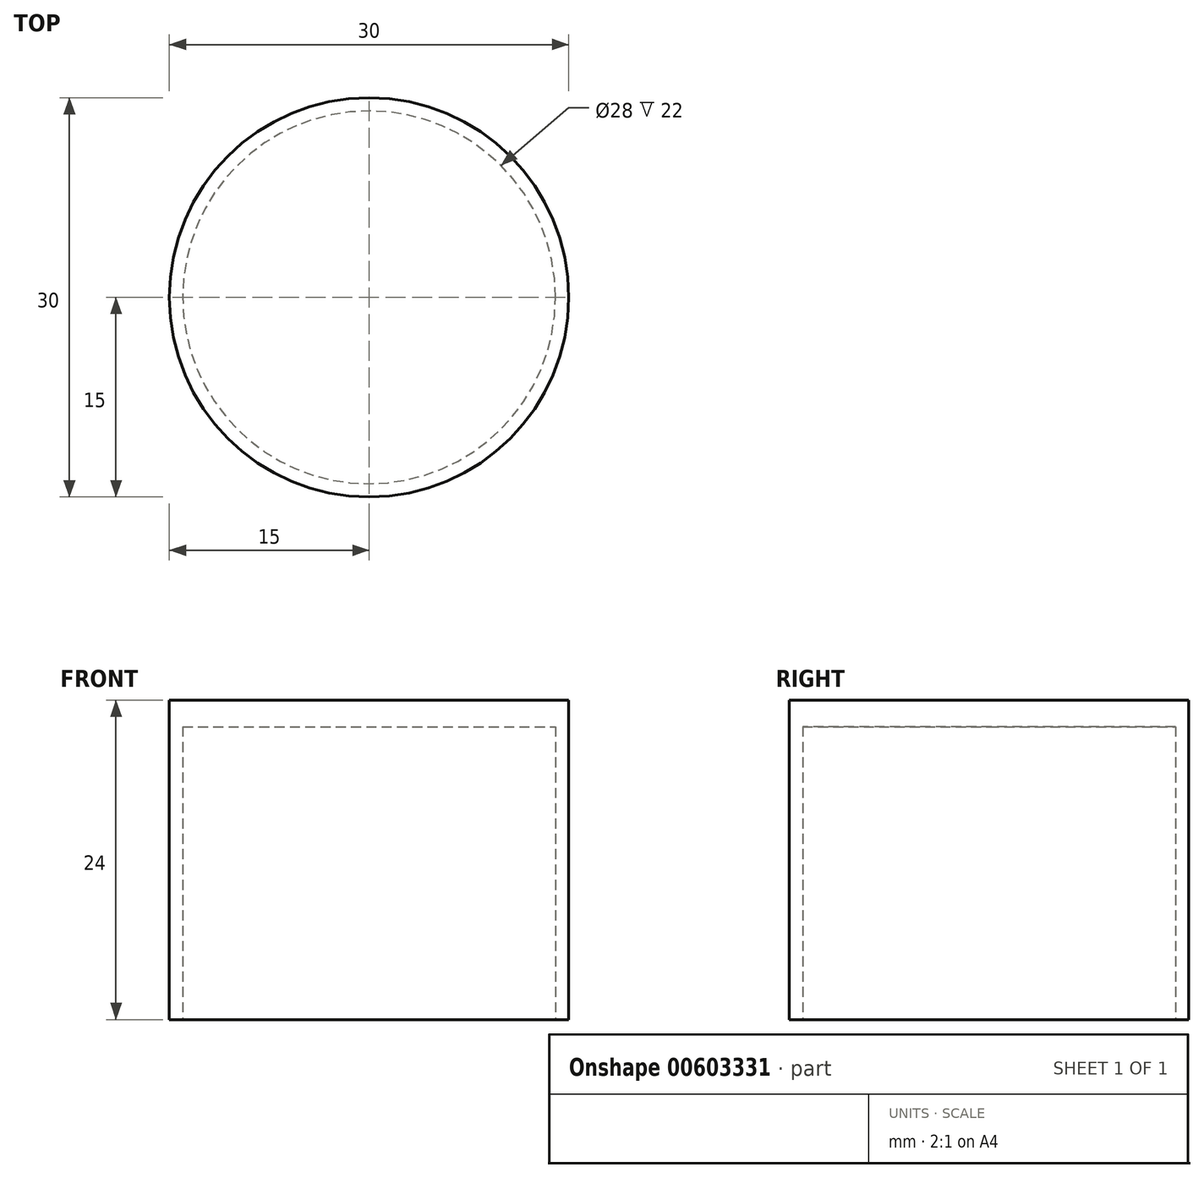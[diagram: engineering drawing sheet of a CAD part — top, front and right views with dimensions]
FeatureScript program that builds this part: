
annotation { "Feature Type Name" : "Feature", "Feature Type Description" : "" }
export const myFeature = defineFeature(function(context is Context, id is Id, definition is map)
    precondition{}
    {
        {
            var Q0;
            Q0=qCreatedBy(makeId("Top.planeOp"),FACE);
            var sketch = newSketch(context, id + "F0", { "sketchPlane" : qUnion([Q0])});
            skCircle(sketch, "E0", {"center": v(0, 0) * mm, "radius": 15 * mm});
            skSolve(sketch);
        }
        {
            var Q0;
            Q0=makeQuery(id+"F0.imprint","IMPRINT",FACE,{"disambiguationData":[TD([[makeQuery(id+"F0.imprint","IMPRINT",EDGE,{"derivedFrom":sQuery(id+"F0.wireOp",EDGE,"E0")}),1.0]])]});
            extrude(context, id + "F1", {"entities" : qUnion([Q0]), "oppositeDirection" : true, "depth" : 24 * mm, "offsetDistance" : 25 * mm});
        }
        {
            var Q0;
            Q0=makeQuery(id+"F1.opExtrude","CAP_FACE",FACE,{"disambiguationData":[OSD([sQuery(id+"F0.wireOp",EDGE,"E0")])],"isStart":false});
            var sketch = newSketch(context, id + "F2", { "sketchPlane" : qUnion([Q0])});
            skCircle(sketch, "E1", {"center": v(0, 0) * mm, "radius": 14 * mm});
            skSolve(sketch);
        }
        {
            var Q0;
            Q0 = qSketchRegion(id + "F2", true);
            extrude(context, id + "F3", {"entities" : qUnion([Q0]), "operationType" : NewBodyOperationType.REMOVE, "oppositeDirection" : true, "depth" : 22 * mm, "offsetDistance" : 25 * mm});
        }
    });
